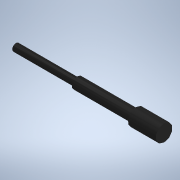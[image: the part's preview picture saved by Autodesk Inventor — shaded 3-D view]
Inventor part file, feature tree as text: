
AUTODESK INVENTOR PART (.ipt)
format: ipt  version: 2022 (Build 260153000, 153)  size: 95,232 bytes
history: native  units: mm (DEFAULTED — no unit token found)
features: other x8, extrude x1, sketch x1
bodies: Solid (feature_tree)
feature tree (10):
  other  "Sólido1"
  other  "Origen"
  extrude  "Extrusión1"  [1 undecoded]
  other  "Plano YZ"
  other  "Plano XZ"
  other  "Plano XY"
  other  "Eje X"
  other  "Eje Y"
  other  "Eje Z"
  sketch  "Boceto1"  dims[d0=170.0mm d1=0.0mm]
note: 1 required parameter value undecoded (feature->parameter linkage not recoverable at this tier; creation-order binding heuristic only, values carry confidence <= 0.55)
